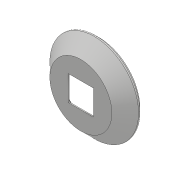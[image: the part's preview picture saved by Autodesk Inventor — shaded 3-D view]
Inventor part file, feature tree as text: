
AUTODESK INVENTOR PART (.ipt)
format: ipt  version: 2017 (Build 210142000, 142)  size: 270,336 bytes
history: native  units: mm
features: sketch x5, fillet x3, extrude x3, revolve x1, shell x1, hole x1, pattern_circular x1, other x1
ambient origin geometry x8: Origin, YZ Plane, XZ Plane, XY Plane, X Axis, Y Axis, Z Axis, Center Point
bodies: Solid1 (feature_tree)
feature tree (16):
  revolve  "Revolution1"  [1 undecoded]
  shell  "Shell1"  Thickness=90.0deg
  fillet  "Fillet1"  Radius=7.0mm
  extrude  "Extrusion1"  TaperAngle=90.0deg  [1 undecoded]
  hole  "Hole1"  [1 undecoded]
  pattern_circular  "Circular Pattern1"  Count=2  [1 undecoded]
  fillet  "Fillet2"  Radius=5.25mm
  fillet  "Fillet3"  Radius=4.5mm
  extrude  "Extrusion2"  Depth=1.75mm
  sketch  "Sketch1"  dims[d1=45.0deg d2=14.0mm d3=90.0deg d4=7.0mm]
  sketch  "Sketch2"  dims[d5=40.0mm d6=90.0deg]
  other  "Srf1"
  sketch  "Sketch3"  dims[d7=1.0mm d8=0.5mm d9=20.0mm d10=0.0mm d11=5.25mm d12=4.5mm]
  sketch  "Sketch4"  dims[d13=0.5mm d14=0.0mm d15=1.75mm]
  sketch  "Sketch5"  dims[d16=1.75mm d17=1.0mm d18=6.0mm d19=4.0mm d20=2.0mm d21=90.0deg d22=8.0mm d23=20.594885mm d24=40.0mm d25=360.0deg d27=1.0mm d28=2.0mm d29=25.0mm d30=25.0mm d31=10.0mm d32=0.0mm]
  extrude  "ExtrusionSrf1"  Depth=10.0mm TaperAngle=360.0deg
note: 4 required parameter values undecoded (feature->parameter linkage not recoverable at this tier; creation-order binding heuristic only, values carry confidence <= 0.55)